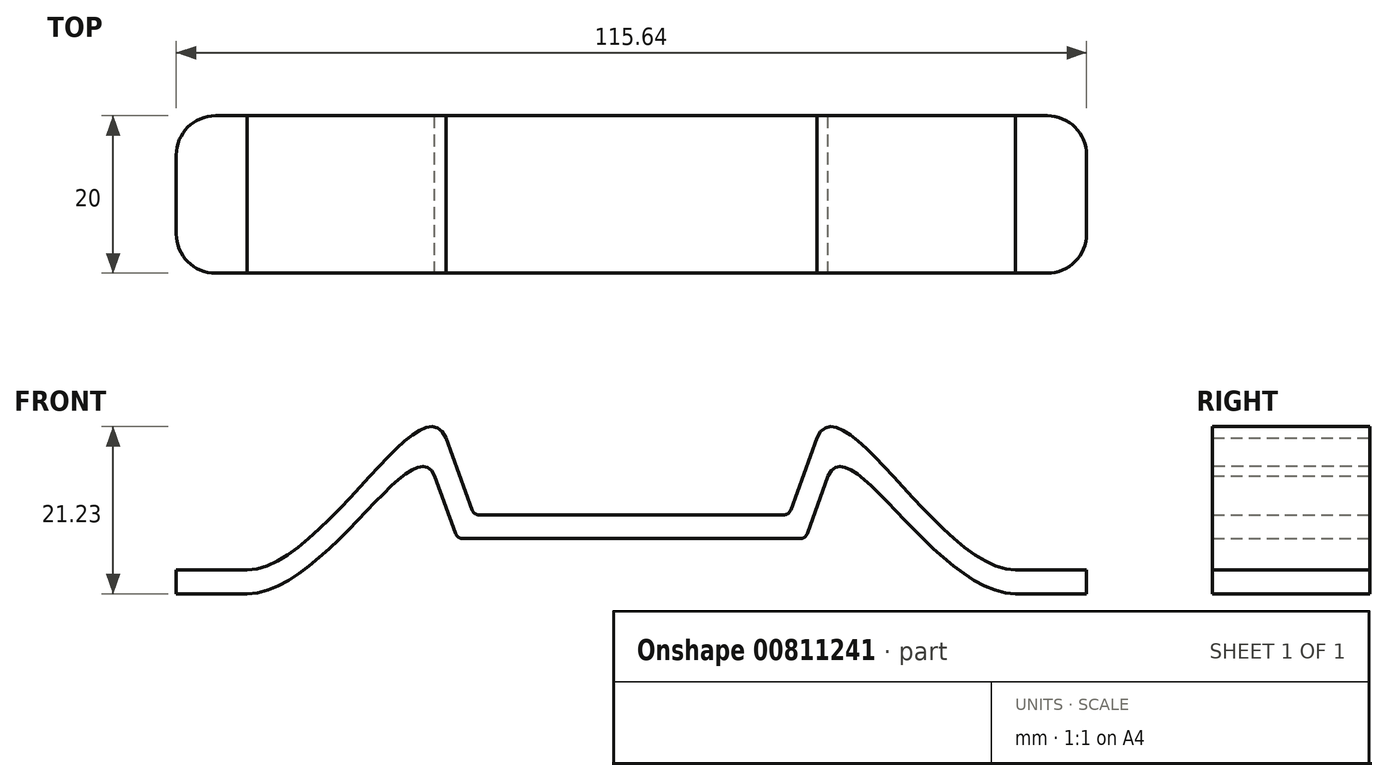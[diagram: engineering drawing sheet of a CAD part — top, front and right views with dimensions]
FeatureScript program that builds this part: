
annotation { "Feature Type Name" : "Feature", "Feature Type Description" : "" }
export const myFeature = defineFeature(function(context is Context, id is Id, definition is map)
    precondition{}
    {
        {
            var Q0;
            Q0=qCreatedBy(makeId("Front.planeOp"),FACE);
            var sketch = newSketch(context, id + "F0", { "sketchPlane" : qUnion([Q0])});
            skLineSegment(sketch, "E0", {"start": v(0, 7) * mm, "end": v(21.4, 7) * mm});
            skLineSegment(sketch, "E1", {"start": v(22.34, 7.66) * mm, "end": v(25, 15) * mm});
            skLineSegment(sketch, "E2", {"start": v(48.8, 0) * mm, "end": v(57.82, 0) * mm});
            skFitSpline(sketch, "E3", {"points": [v(25, 15) * mm, v(48.8, 0) * mm], "startDerivative": vector(8.3, 19.17) * mm, "endDerivative": vector(29.89, -0.22) * mm});
            skLineSegment(sketch, "E4.1", {"start": v(20.24, 10.66) * mm, "end": v(23.55, 19.82) * mm});
            skLineSegment(sketch, "E4.2", {"start": v(0, 10) * mm, "end": v(19.3, 10) * mm});
            skLineSegment(sketch, "E5", {"start": v(57.82, 0) * mm, "end": v(57.82, 3) * mm});
            skLineSegment(sketch, "E6", {"start": v(57.82, 3) * mm, "end": v(48.8, 3) * mm});
            skPoint(sketch, "E7.visualSharp", {"position": v(20, 10) * mm});
            skArc(sketch, "E7.filletArc", {"start": v(19.3, 10) * mm, "mid": v(19.87, 10.18) * mm, "end": v(20.24, 10.66) * mm});
            skPoint(sketch, "E8.visualSharp", {"position": v(22.1, 7) * mm});
            skArc(sketch, "E8.filletArc", {"start": v(21.4, 7) * mm, "mid": v(21.98, 7.18) * mm, "end": v(22.34, 7.66) * mm});
            skArc(sketch, "E9.MirrorCS", {"start": v(-19.3, 10) * mm, "mid": v(-19.87, 10.18) * mm, "end": v(-20.24, 10.66) * mm});
            skArc(sketch, "E10.MirrorCS", {"start": v(-21.4, 7) * mm, "mid": v(-21.98, 7.18) * mm, "end": v(-22.34, 7.66) * mm});
            skLineSegment(sketch, "E11.MirrorCS", {"start": v(0, 7) * mm, "end": v(-21.4, 7) * mm});
            skPoint(sketch, "E12.MirrorP", {"position": v(-20, 10) * mm});
            skLineSegment(sketch, "E13.MirrorCS", {"start": v(0, 10) * mm, "end": v(-19.3, 10) * mm});
            skLineSegment(sketch, "E14.MirrorCS", {"start": v(-48.8, 0) * mm, "end": v(-57.82, 0) * mm});
            skLineSegment(sketch, "E15.MirrorCS", {"start": v(-57.82, 3) * mm, "end": v(-48.8, 3) * mm});
            skLineSegment(sketch, "E16.MirrorCS", {"start": v(-57.82, 0) * mm, "end": v(-57.82, 3) * mm});
            skPoint(sketch, "E17.MirrorP", {"position": v(-22.1, 7) * mm});
            skFitSpline(sketch, "E18.MirrorCS", {"points": [v(-25, 15) * mm, v(-48.8, 0) * mm], "startDerivative": vector(-8.3, 19.17) * mm, "endDerivative": vector(-29.89, -0.22) * mm});
            skLineSegment(sketch, "E19.MirrorCS", {"start": v(-20.24, 10.66) * mm, "end": v(-23.55, 19.82) * mm});
            skLineSegment(sketch, "E20.MirrorCS", {"start": v(-22.34, 7.66) * mm, "end": v(-25, 15) * mm});
            skFitSpline(sketch, "E21", {"points": [v(-23.55, 19.82) * mm, v(-48.8, 3) * mm], "startDerivative": vector(-10.06, 22.2) * mm, "endDerivative": vector(-28.53, -0.38) * mm});
            skFitSpline(sketch, "E22.MirrorCS", {"points": [v(23.55, 19.82) * mm, v(48.8, 3) * mm], "startDerivative": vector(10.06, 22.2) * mm, "endDerivative": vector(28.53, -0.38) * mm});
            skSolve(sketch);
        }
        {
            var Q0;
            Q0=makeQuery(id+"F0.imprint","IMPRINT",FACE,{"disambiguationData":[TD([[makeQuery(id+"F0.imprint","IMPRINT",EDGE,{"derivedFrom":sQuery(id+"F0.wireOp",EDGE,"E0")}),1.0]])]});
            extrude(context, id + "F1", {"entities" : qUnion([Q0]), "endBound" : BoundingType.SYMMETRIC, "depth" : 20 * mm, "offsetDistance" : 25 * mm});
        }
        {
            var Q0;
            Q0=makeQuery(id+"F1.opExtrude","CAP_EDGE",EDGE,{"disambiguationData":[OSD([sQuery(id+"F0.wireOp",EDGE,"E5")])],"isStart":false});
            var Q1;
            Q1=makeQuery(id+"F1.opExtrude","CAP_EDGE",EDGE,{"disambiguationData":[OSD([sQuery(id+"F0.wireOp",EDGE,"E5")])],"isStart":true});
            var Q2;
            Q2=makeQuery(id+"F1.opExtrude","CAP_EDGE",EDGE,{"disambiguationData":[OSD([sQuery(id+"F0.wireOp",EDGE,"E16.MirrorCS")])],"isStart":true});
            var Q3;
            Q3=makeQuery(id+"F1.opExtrude","CAP_EDGE",EDGE,{"disambiguationData":[OSD([sQuery(id+"F0.wireOp",EDGE,"E16.MirrorCS")])],"isStart":false});
            fillet(context, id + "F2", {"entities" : qUnion([Q0, Q1, Q2, Q3]), "radius" : 5 * mm, "tangentPropagation" : true, "allowEdgeOverflow" : false});
        }
    });
